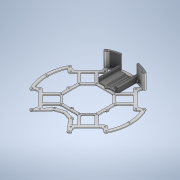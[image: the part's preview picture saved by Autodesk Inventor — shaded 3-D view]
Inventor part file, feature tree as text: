
AUTODESK INVENTOR PART (.ipt)
format: ipt  version: 2020 (Build 240168000, 168)  size: 1,817,088 bytes
history: native  units: mm
features: projected_geometry x33, extrude x18, sketch x12, other x4, fillet x3, chamfer x1
ambient origin geometry x8: Origin, YZ Plane, XZ Plane, XY Plane, X Axis, Y Axis, Z Axis, Center Point
bodies: Body1 (feature_tree)
feature tree (71):
  other  "Твердое тело1"
  extrude  "outer"  TaperAngle=45.0deg  [1 undecoded]
  extrude  "inner"  Depth=7.0mm
  sketch  "Эскиз3"
  extrude  "Выдавливание3"  Depth=20.0mm
  extrude  "Выдавливание4"  Depth=7.0mm
  sketch  "Эскиз4"
  extrude  "Выдавливание5"  Depth=3.2mm
  extrude  "Выдавливание6"  Depth=59.0mm
  sketch  "Эскиз5"
  extrude  "Выдавливание7"  Depth=83.0mm
  extrude  "Выдавливание8"  Depth=69.0mm
  sketch  "Эскиз6"
  extrude  "Выдавливание9"  Depth=55.0mm
  extrude  "Выдавливание10"  Depth=3.0mm
  other  "РабПлоскость1"
  extrude  "Выдавливание11"  Depth=8.0mm
  chamfer  "Фаска1"  Distance=5.0mm
  fillet  "Сопряжение1"  Radius=2.0mm
  fillet  "Сопряжение2"  Radius=40.0mm
  other  "РабПлоскость2"
  extrude  "Выдавливание12"  Depth=2.0mm
  sketch  "Эскиз9"
  extrude  "Выдавливание13"  Depth=105.0mm
  extrude  "Выдавливание14"  Depth=2.0mm
  other  "РабПлоскость3"
  extrude  "Выдавливание15"  Depth=2.0mm TaperAngle=0.0deg
  extrude  "Выдавливание16"  Depth=3.5mm
  fillet  "Сопряжение3"  Radius=2.0mm
  extrude  "Выдавливание17"  Depth=6.0mm
  extrude  "Выдавливание18"  Depth=12.0mm
  sketch  "Эскиз1"
  sketch  "Эскиз2"
  projected_geometry  "Спроецированная петля1"
  projected_geometry  "Спроецированная петля2"
  projected_geometry  "Спроецированная петля3"
  projected_geometry  "Спроецированная петля4"
  projected_geometry  "Спроецированная петля5"
  sketch  "Эскиз7"
  projected_geometry  "Спроецированная петля6"
  projected_geometry  "Спроецированная петля7"
  projected_geometry  "Спроецированная петля8"
  sketch  "Эскиз8"
  projected_geometry  "Спроецированная петля9"
  projected_geometry  "Спроецированная петля10"
  projected_geometry  "Спроецированная петля11"
  projected_geometry  "Спроецированная петля12"
  projected_geometry  "Спроецированная петля13"
  projected_geometry  "Спроецированная петля14"
  projected_geometry  "Спроецированная петля15"
  sketch  "Эскиз10"
  projected_geometry  "Спроецированная петля16"
  projected_geometry  "Спроецированная петля17"
  projected_geometry  "Спроецированная петля18"
  projected_geometry  "Спроецированная петля19"
  projected_geometry  "Спроецированная петля20"
  projected_geometry  "Спроецированная петля21"
  projected_geometry  "Спроецированная петля22"
  projected_geometry  "Спроецированная петля23"
  projected_geometry  "Спроецированная петля24"
  projected_geometry  "Спроецированная петля25"
  sketch  "Эскиз11"
  sketch  "Эскиз12"
  projected_geometry  "Спроецированная петля26"
  projected_geometry  "Спроецированная петля27"
  projected_geometry  "Спроецированная петля28"
  projected_geometry  "Спроецированная петля29"
  projected_geometry  "Спроецированная петля30"
  projected_geometry  "Спроецированная петля31"
  projected_geometry  "Спроецированная петля32"
  projected_geometry  "Спроецированная петля33"
note: 1 required parameter value undecoded (feature->parameter linkage not recoverable at this tier; creation-order binding heuristic only, values carry confidence <= 0.55)
